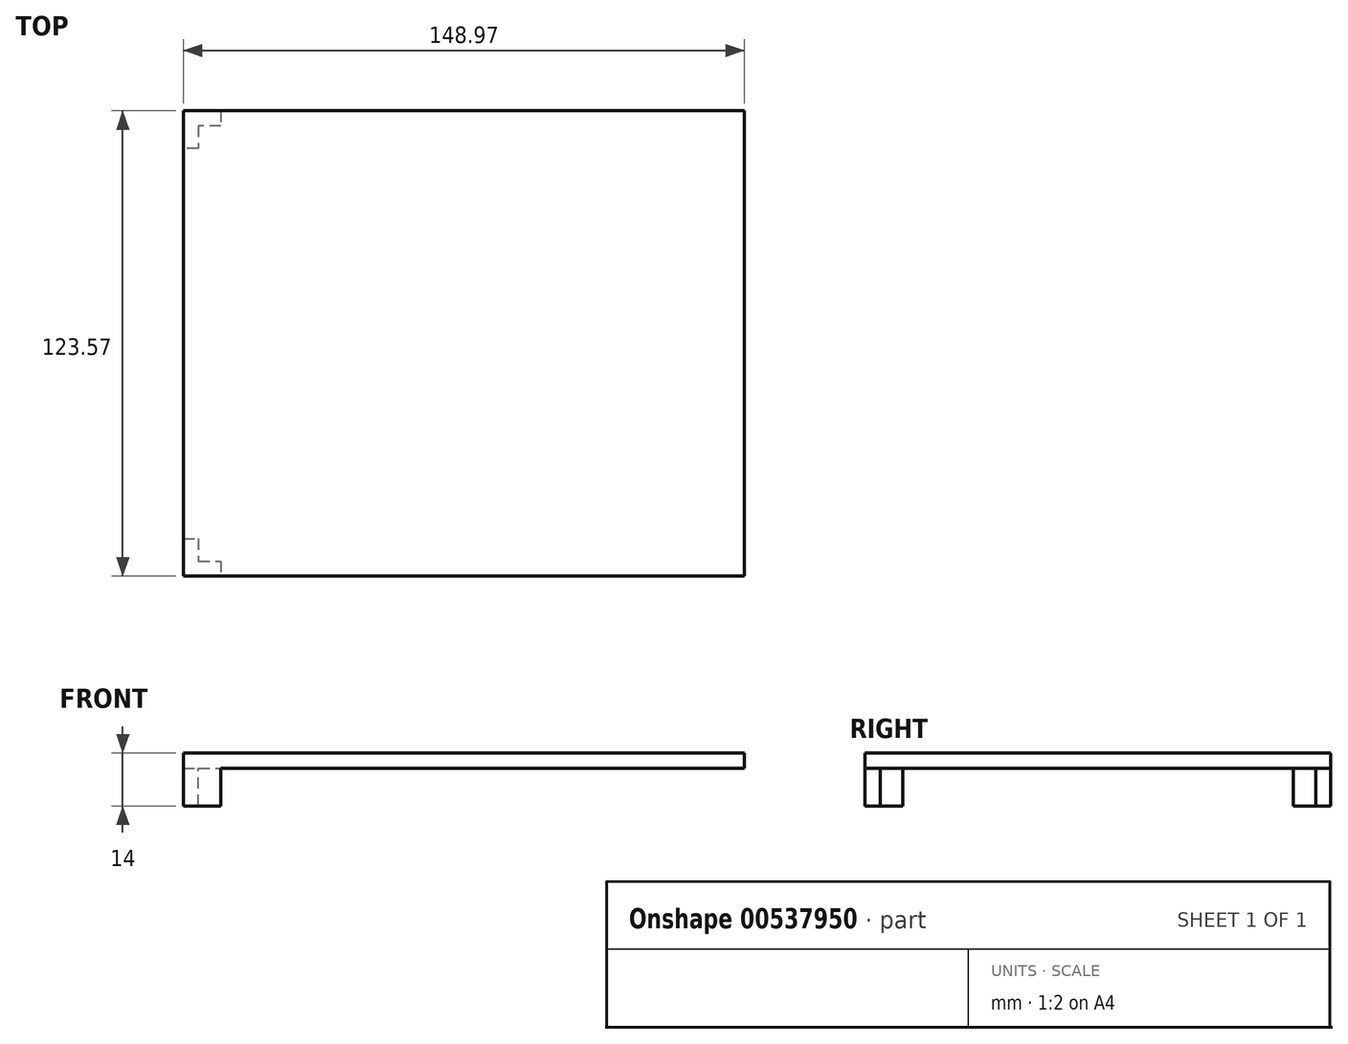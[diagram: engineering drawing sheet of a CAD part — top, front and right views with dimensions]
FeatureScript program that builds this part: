
annotation { "Feature Type Name" : "Feature", "Feature Type Description" : "" }
export const myFeature = defineFeature(function(context is Context, id is Id, definition is map)
    precondition{}
    {
        {
            var Q0;
            Q0=qCreatedBy(makeId("Top.planeOp"),FACE);
            var sketch = newSketch(context, id + "F0", { "sketchPlane" : qUnion([Q0])});
            skLineSegment(sketch, "E0.bottom", {"start": v(0, 0) * mm, "end": v(140.97, 0) * mm, "construction": true});
            skLineSegment(sketch, "E0.top", {"start": v(0, -115.57) * mm, "end": v(140.97, -115.57) * mm, "construction": true});
            skLineSegment(sketch, "E0.left", {"start": v(0, 0) * mm, "end": v(0, -115.57) * mm, "construction": true});
            skLineSegment(sketch, "E0.right", {"start": v(140.97, 0) * mm, "end": v(140.97, -115.57) * mm, "construction": true});
            skLineSegment(sketch, "E1.bottom", {"start": v(-4, 4) * mm, "end": v(144.97, 4) * mm});
            skLineSegment(sketch, "E1.top", {"start": v(-4, -119.57) * mm, "end": v(144.97, -119.57) * mm});
            skLineSegment(sketch, "E1.left", {"start": v(-4, 4) * mm, "end": v(-4, -119.57) * mm});
            skLineSegment(sketch, "E1.right", {"start": v(144.97, 4) * mm, "end": v(144.97, -119.57) * mm});
            skLineSegment(sketch, "E2.bottom", {"start": v(4, -4) * mm, "end": v(136.97, -4) * mm});
            skLineSegment(sketch, "E2.top", {"start": v(4, -111.57) * mm, "end": v(136.97, -111.57) * mm});
            skLineSegment(sketch, "E2.left", {"start": v(4, -4) * mm, "end": v(4, -111.57) * mm});
            skLineSegment(sketch, "E2.right", {"start": v(136.97, -4) * mm, "end": v(136.97, -111.57) * mm});
            skLineSegment(sketch, "E3", {"start": v(70.48, 0) * mm, "end": v(70.48, -115.57) * mm, "construction": true});
            skLineSegment(sketch, "E4", {"start": v(0, -57.79) * mm, "end": v(140.97, -57.79) * mm, "construction": true});
            skPoint(sketch, "E5", {"position": v(4, -57.79) * mm});
            skPoint(sketch, "E6", {"position": v(-4, -57.79) * mm});
            skPoint(sketch, "E7", {"position": v(136.97, -57.79) * mm});
            skPoint(sketch, "E8", {"position": v(144.97, -57.79) * mm});
            skLineSegment(sketch, "E9", {"start": v(70.48, -115.57) * mm, "end": v(70.48, -119.57) * mm, "construction": true});
            skLineSegment(sketch, "E10", {"start": v(140.97, -57.79) * mm, "end": v(144.97, -57.79) * mm, "construction": true});
            skLineSegment(sketch, "E11", {"start": v(136.97, -111.57) * mm, "end": v(140.97, -111.57) * mm, "construction": true});
            skLineSegment(sketch, "E12", {"start": v(136.97, -111.57) * mm, "end": v(136.97, -115.57) * mm, "construction": true});
            skLineSegment(sketch, "E13", {"start": v(4, -111.57) * mm, "end": v(0, -111.57) * mm, "construction": true});
            skLineSegment(sketch, "E14", {"start": v(0, -111.57) * mm, "end": v(-4, -111.57) * mm, "construction": true});
            skSolve(sketch);
        }
        {
            var Q0;
            Q0 = qSketchRegion(id + "F0", true);
            extrude(context, id + "F1", {"entities" : qUnion([Q0]), "depth" : 4 * mm, "offsetDistance" : 25 * mm});
        }
        {
            var Q0;
            Q0=makeQuery(id+"F1.opExtrude","CAP_FACE",FACE,{"disambiguationData":[OSD([sQuery(id+"F0.wireOp",EDGE,"E1.bottom"),sQuery(id+"F0.wireOp",EDGE,"E1.top"),sQuery(id+"F0.wireOp",EDGE,"E1.left"),sQuery(id+"F0.wireOp",EDGE,"E1.right"),sQuery(id+"F0.wireOp",EDGE,"E2.bottom"),sQuery(id+"F0.wireOp",EDGE,"E2.top"),sQuery(id+"F0.wireOp",EDGE,"E2.left"),sQuery(id+"F0.wireOp",EDGE,"E2.right")])],"isStart":true});
            var sketch = newSketch(context, id + "F2", { "sketchPlane" : qUnion([Q0])});
            skLineSegment(sketch, "E15.bottom", {"start": v(144.97, 62.78) * mm, "end": v(140.97, 62.78) * mm, "construction": true});
            skLineSegment(sketch, "E15.top", {"start": v(144.97, 52.78) * mm, "end": v(140.97, 52.78) * mm, "construction": true});
            skLineSegment(sketch, "E15.left", {"start": v(144.97, 62.78) * mm, "end": v(144.97, 52.79) * mm, "construction": true});
            skLineSegment(sketch, "E15.right", {"start": v(140.97, 62.78) * mm, "end": v(140.97, 52.79) * mm, "construction": true});
            skLineSegment(sketch, "E16.bottom", {"start": v(-4, 62.78) * mm, "end": v(0, 62.78) * mm, "construction": true});
            skLineSegment(sketch, "E16.top", {"start": v(-4, 52.78) * mm, "end": v(0, 52.78) * mm, "construction": true});
            skLineSegment(sketch, "E16.left", {"start": v(-4, 62.78) * mm, "end": v(-4, 52.78) * mm, "construction": true});
            skLineSegment(sketch, "E16.right", {"start": v(0, 62.78) * mm, "end": v(0, 52.78) * mm, "construction": true});
            skLineSegment(sketch, "E17.bottom", {"start": v(65.49, 119.57) * mm, "end": v(75.49, 119.57) * mm, "construction": true});
            skLineSegment(sketch, "E17.top", {"start": v(65.49, 115.57) * mm, "end": v(75.49, 115.57) * mm, "construction": true});
            skLineSegment(sketch, "E17.left", {"start": v(65.49, 119.57) * mm, "end": v(65.49, 115.57) * mm, "construction": true});
            skLineSegment(sketch, "E17.right", {"start": v(75.49, 119.57) * mm, "end": v(75.49, 115.57) * mm, "construction": true});
            skLineSegment(sketch, "E18.bottom", {"start": v(65.49, -4) * mm, "end": v(75.49, -4) * mm, "construction": true});
            skLineSegment(sketch, "E18.top", {"start": v(65.49, 0) * mm, "end": v(75.49, 0) * mm, "construction": true});
            skLineSegment(sketch, "E18.left", {"start": v(65.49, -4) * mm, "end": v(65.49, 0) * mm, "construction": true});
            skLineSegment(sketch, "E18.right", {"start": v(75.49, -4) * mm, "end": v(75.49, 0) * mm, "construction": true});
            skLineSegment(sketch, "E19", {"start": v(-4, 119.57) * mm, "end": v(-4, 109.57) * mm});
            skLineSegment(sketch, "E20", {"start": v(-4, 109.57) * mm, "end": v(0, 109.57) * mm});
            skLineSegment(sketch, "E21", {"start": v(0, 109.57) * mm, "end": v(0, 115.57) * mm});
            skLineSegment(sketch, "E22", {"start": v(0, 115.57) * mm, "end": v(6, 115.57) * mm});
            skLineSegment(sketch, "E23", {"start": v(6, 115.57) * mm, "end": v(6, 119.57) * mm});
            skLineSegment(sketch, "E24", {"start": v(6, 119.57) * mm, "end": v(-4, 119.57) * mm});
            skLineSegment(sketch, "E25", {"start": v(0, 0) * mm, "end": v(0, 6) * mm});
            skLineSegment(sketch, "E26", {"start": v(0, 6) * mm, "end": v(-4, 6) * mm});
            skLineSegment(sketch, "E27", {"start": v(-4, 6) * mm, "end": v(-4, -4) * mm});
            skLineSegment(sketch, "E28", {"start": v(-4, -4) * mm, "end": v(6, -4) * mm});
            skLineSegment(sketch, "E29", {"start": v(6, -4) * mm, "end": v(6, 0) * mm});
            skLineSegment(sketch, "E30", {"start": v(6, 0) * mm, "end": v(0, 0) * mm});
            skSolve(sketch);
        }
        {
            var Q0;
            Q0=makeQuery(id+"F1.opExtrude","CAP_FACE",FACE,{"disambiguationData":[OSD([sQuery(id+"F0.wireOp",EDGE,"E1.bottom"),sQuery(id+"F0.wireOp",EDGE,"E1.top"),sQuery(id+"F0.wireOp",EDGE,"E1.left"),sQuery(id+"F0.wireOp",EDGE,"E1.right"),sQuery(id+"F0.wireOp",EDGE,"E2.bottom"),sQuery(id+"F0.wireOp",EDGE,"E2.top"),sQuery(id+"F0.wireOp",EDGE,"E2.left"),sQuery(id+"F0.wireOp",EDGE,"E2.right")])],"isStart":false});
            var sketch = newSketch(context, id + "F3", { "sketchPlane" : qUnion([Q0])});
            skCircle(sketch, "E31", {"center": v(70.48, -57.79) * mm, "radius": 14 * mm});
            skArc(sketch, "E32", {"start": v(50.89, -61.79) * mm, "mid": v(56.34, -71.93) * mm, "end": v(66.49, -77.38) * mm});
            skLineSegment(sketch, "E33.bottom", {"start": v(66.48, -4) * mm, "end": v(74.49, -4) * mm});
            skLineSegment(sketch, "E33.top", {"start": v(66.48, -111.57) * mm, "end": v(74.49, -111.57) * mm});
            skLineSegment(sketch, "E33.left", {"start": v(66.48, -4) * mm, "end": v(66.48, -38.19) * mm});
            skLineSegment(sketch, "E33.right", {"start": v(74.49, -4) * mm, "end": v(74.49, -38.19) * mm});
            skLineSegment(sketch, "E34.bottom", {"start": v(136.97, -53.78) * mm, "end": v(90.08, -53.78) * mm});
            skLineSegment(sketch, "E34.top", {"start": v(136.97, -61.79) * mm, "end": v(90.08, -61.79) * mm});
            skLineSegment(sketch, "E34.left", {"start": v(136.97, -53.78) * mm, "end": v(136.97, -61.78) * mm});
            skLineSegment(sketch, "E34.right", {"start": v(4, -53.78) * mm, "end": v(4, -61.79) * mm});
            skPoint(sketch, "E35", {"position": v(70.48, -111.57) * mm});
            skLineSegment(sketch, "E36.trimOffspring", {"start": v(74.49, -77.38) * mm, "end": v(74.49, -111.57) * mm});
            skLineSegment(sketch, "E37.trimOffspring", {"start": v(66.48, -77.38) * mm, "end": v(66.48, -111.57) * mm});
            skLineSegment(sketch, "E38.trimOffspring", {"start": v(50.89, -61.79) * mm, "end": v(4, -61.79) * mm});
            skLineSegment(sketch, "E39.trimOffspring", {"start": v(50.89, -53.78) * mm, "end": v(4, -53.78) * mm});
            skArc(sketch, "E40.trimOffspring", {"start": v(66.49, -38.19) * mm, "mid": v(56.34, -43.64) * mm, "end": v(50.89, -53.79) * mm});
            skArc(sketch, "E41.trimOffspring", {"start": v(90.08, -53.78) * mm, "mid": v(84.63, -43.64) * mm, "end": v(74.48, -38.19) * mm});
            skArc(sketch, "E42.trimOffspring", {"start": v(74.48, -77.38) * mm, "mid": v(84.63, -71.93) * mm, "end": v(90.08, -61.79) * mm});
            skSolve(sketch);
        }
        {
            var Q0;
            Q0 = qSketchRegion(id + "F2", true);
            extrude(context, id + "F4", {"entities" : qUnion([Q0]), "operationType" : NewBodyOperationType.ADD, "depth" : 10 * mm, "offsetDistance" : 25 * mm});
        }
        {
            var Q0;
            Q0=sQuery(id+"F0.wireOp",EDGE,"E3");
            cPlane(context, id + "F5", {"entities" : qUnion([Q0]), "cplaneType" : CPlaneType.LINE_ANGLE, "offset" : 25 * mm, "angle" : 90 * degree, "width" : 150 * mm, "height" : 150 * mm});
        }
        {
            var Q0;
            Q0=makeQuery(id+"F1.opExtrude","CAP_FACE",FACE,{"disambiguationData":[OSD([sQuery(id+"F0.wireOp",EDGE,"E1.bottom"),sQuery(id+"F0.wireOp",EDGE,"E1.top"),sQuery(id+"F0.wireOp",EDGE,"E1.left"),sQuery(id+"F0.wireOp",EDGE,"E1.right"),sQuery(id+"F0.wireOp",EDGE,"E2.bottom"),sQuery(id+"F0.wireOp",EDGE,"E2.top"),sQuery(id+"F0.wireOp",EDGE,"E2.left"),sQuery(id+"F0.wireOp",EDGE,"E2.right")])],"isStart":false});
            var sketch = newSketch(context, id + "F6", { "sketchPlane" : qUnion([Q0])});
            skLineSegment(sketch, "E43.bottom", {"start": v(4, -4) * mm, "end": v(136.97, -4) * mm});
            skLineSegment(sketch, "E43.top", {"start": v(4, -111.57) * mm, "end": v(136.97, -111.57) * mm});
            skLineSegment(sketch, "E43.left", {"start": v(4, -4) * mm, "end": v(4, -111.57) * mm});
            skLineSegment(sketch, "E43.right", {"start": v(136.97, -4) * mm, "end": v(136.97, -111.57) * mm});
            skSolve(sketch);
        }
        {
            var Q0;
            Q0 = qSketchRegion(id + "F6", true);
            var Q1;
            Q1=makeQuery(id+"F1.opExtrude","CAP_FACE",FACE,{"disambiguationData":[OSD([sQuery(id+"F0.wireOp",EDGE,"E1.bottom"),sQuery(id+"F0.wireOp",EDGE,"E1.top"),sQuery(id+"F0.wireOp",EDGE,"E1.left"),sQuery(id+"F0.wireOp",EDGE,"E1.right"),sQuery(id+"F0.wireOp",EDGE,"E2.bottom"),sQuery(id+"F0.wireOp",EDGE,"E2.top"),sQuery(id+"F0.wireOp",EDGE,"E2.left"),sQuery(id+"F0.wireOp",EDGE,"E2.right")])],"isStart":true});
            extrude(context, id + "F7", {"entities" : qUnion([Q0]), "operationType" : NewBodyOperationType.ADD, "endBound" : BoundingType.UP_TO_SURFACE, "oppositeDirection" : true, "depth" : 25 * mm, "endBoundEntityFace" : qUnion([Q1]), "offsetDistance" : 25 * mm});
        }
    });
